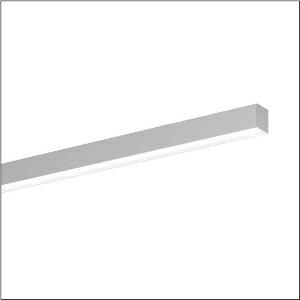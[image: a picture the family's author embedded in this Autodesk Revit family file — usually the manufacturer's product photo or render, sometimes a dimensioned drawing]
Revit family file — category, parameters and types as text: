
# Revit family: silica_r__21_51mx23db45sb_b235
name_source: partatom
category: Lighting Fixtures
units: mm (PartAtom-declared; Revit-internal decimal feet)

## family parameters
Cut with Voids When Loaded = No
Host = Face
Light Source = No
Part Type = Normal
Room Calculation Point = No
Round Connector Dimension = Use Diameter
Shared = No

## types (1)
- --- (1 x LED, 4100 lm, 28.1 W, 4000K)
    Apparent Load = 28 VA
    CIE Flux Codes = 78 96 99 100 100
    Color Rendering = 80
    Color Temperature = 4000K
    Default Elevation = 1800 mm
    Description = Silica® 21, office luminaire, primary optical cover: prismatic diffuser, of PMMA, CAT 2 (L<= 3000cd/m²), light emission: direct distribution, primary light characteristic: symmetric, installation type: surface-mounted, LED, rated luminous flux: 4.100lm, luminous efficacy: 146lm/W, light colour: 840, colour temperature: 4000K, with terminal, 3+2-pole, max. 2.5mm², mains connection: 220..240V, AC, 50/60Hz, rated input power: 28.1W, luminaire housing, of aluminium, metallic grey (RAL 9006), length: 1.504mm, width: 53mm, height: 53mm, protection rating (complete): IP20, insulation class (complete): insulation class I (protective earthing), certification: CE, permissible operating ambient temperature: 0..+35°C, standard: EN 50419, packaging unit: 1 piece
    Height = 0 mm  [stored 0 ft]
    Lamp = 1 x LED
    Lamp Light Flux = 4100 lm
    Lamp Power = 28.1 W
    Lamp count = 1
    Length = 1504 mm
    Luminous efficacy = 146 lm/W
    Manufacturer = Siteco
    ModVariant = No
    Model = 51MX23DB45SB
    Mounting Place = Ceiling
    Mounting Type = Recessed
    Number of Poles = 1
    OnlyDefault = Yes
    Power Factor = 1
    Product Name = Silica® 21
    Product group = office luminaire | ceiling recessed
    ProductGroupID = 401
    Protection Class = Protection class I
    Protection Degree = IP 20
    RLX_Detail_Level = 1
    RLX_Emergency_Light_Flux = 0 lm
    RLX_Emergency_Type = 0
    RLX_Emergency_Type_DB = No
    RlxData = <blob elided: 21313 chars, md5=54c9c7a2>
    Socket = socket
    Standby Power = 0 W
    System Light Flux = 4100 lm
    System Power = 28 W
    Type Comments = factory setting: luminous flux: 100 % | dim-lin: 254 | 323 mA
    Type Image = l_1313588.jpg
    URL = http://relux.com
    VarID = @adj_067855
    Voltage = 0 V
    Weight = 0.00 kg
    Width = 53 mm

note: [stored X ft] marks values corroborated as IEEE doubles in the binary element streams (Revit-internal decimal feet)

## geometry (parser evidence)
native form markers: Blend x4, Sweep x10
no freeform markers — native parametric forms only
